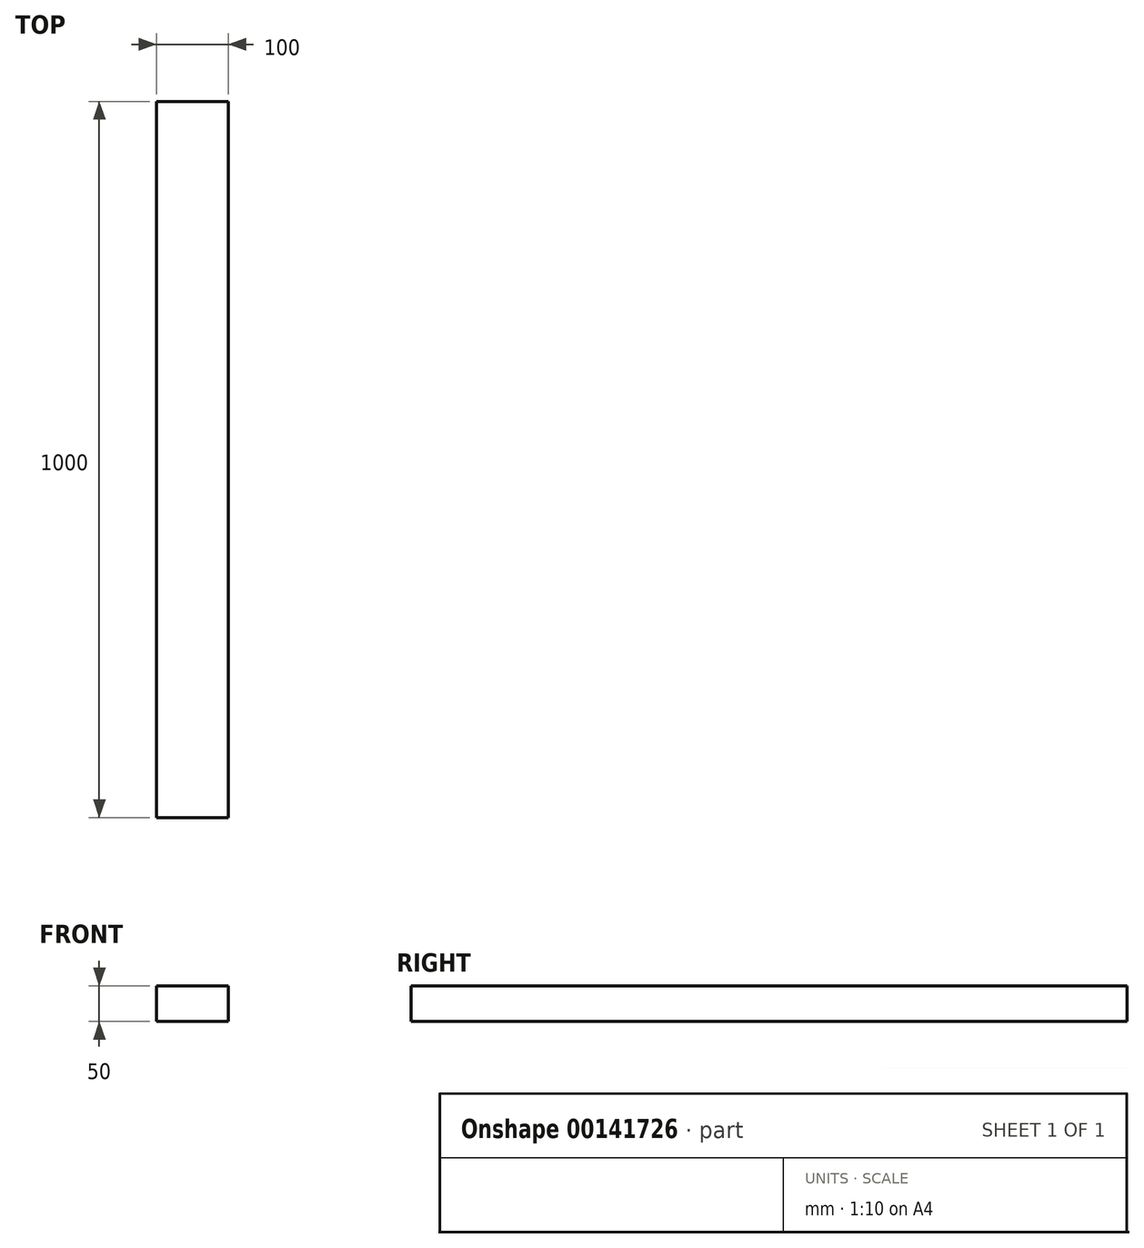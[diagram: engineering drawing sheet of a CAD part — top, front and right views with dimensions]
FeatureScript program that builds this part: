
annotation { "Feature Type Name" : "Feature", "Feature Type Description" : "" }
export const myFeature = defineFeature(function(context is Context, id is Id, definition is map)
    precondition{}
    {
        {
            var Q0;
            Q0=qCreatedBy(makeId("Front.planeOp"),FACE);
            var sketch = newSketch(context, id + "F0", { "sketchPlane" : qUnion([Q0])});
            skLineSegment(sketch, "E0.bottom", {"start": v(-50, 25) * mm, "end": v(50, 25) * mm});
            skLineSegment(sketch, "E0.top", {"start": v(-50, -25) * mm, "end": v(50, -25) * mm});
            skLineSegment(sketch, "E0.left", {"start": v(-50, 25) * mm, "end": v(-50, -25) * mm});
            skLineSegment(sketch, "E0.right", {"start": v(50, 25) * mm, "end": v(50, -25) * mm});
            skPoint(sketch, "E0.middle", {"position": v(0, 0) * mm});
            skSolve(sketch);
        }
        {
            var Q0;
            Q0=makeQuery(id+"F0.imprint","IMPRINT",FACE,{"disambiguationData":[TD([[makeQuery(id+"F0.imprint","IMPRINT",EDGE,{"derivedFrom":sQuery(id+"F0.wireOp",EDGE,"E0.bottom")}),-1.0]])]});
            extrude(context, id + "F1", {"entities" : qUnion([Q0]), "depth" : 1000 * mm});
        }
    });
